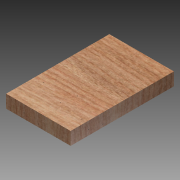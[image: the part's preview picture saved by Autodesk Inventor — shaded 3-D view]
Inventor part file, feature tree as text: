
AUTODESK INVENTOR PART (.ipt)
format: ipt  version: 2014 SP1 (Build 180222100, 222)  size: 92,672 bytes
history: native  units: in
note: dims shown in document units (in); Inventor stores cm internally (conversion verified against a paired STEP export)
features: extrude x1, sketch x1
ambient origin geometry x8: Origin, YZ Plane, XZ Plane, XY Plane, X Axis, Y Axis, Z Axis, Center Point
bodies: Solid1 (feature_tree)
feature tree (2):
  extrude  "Extrusion1"  Depth=8.0in
  sketch  "Sketch1"  dims[d0=5.0in d1=8.0in d2=1.0in d3=0.0in]
